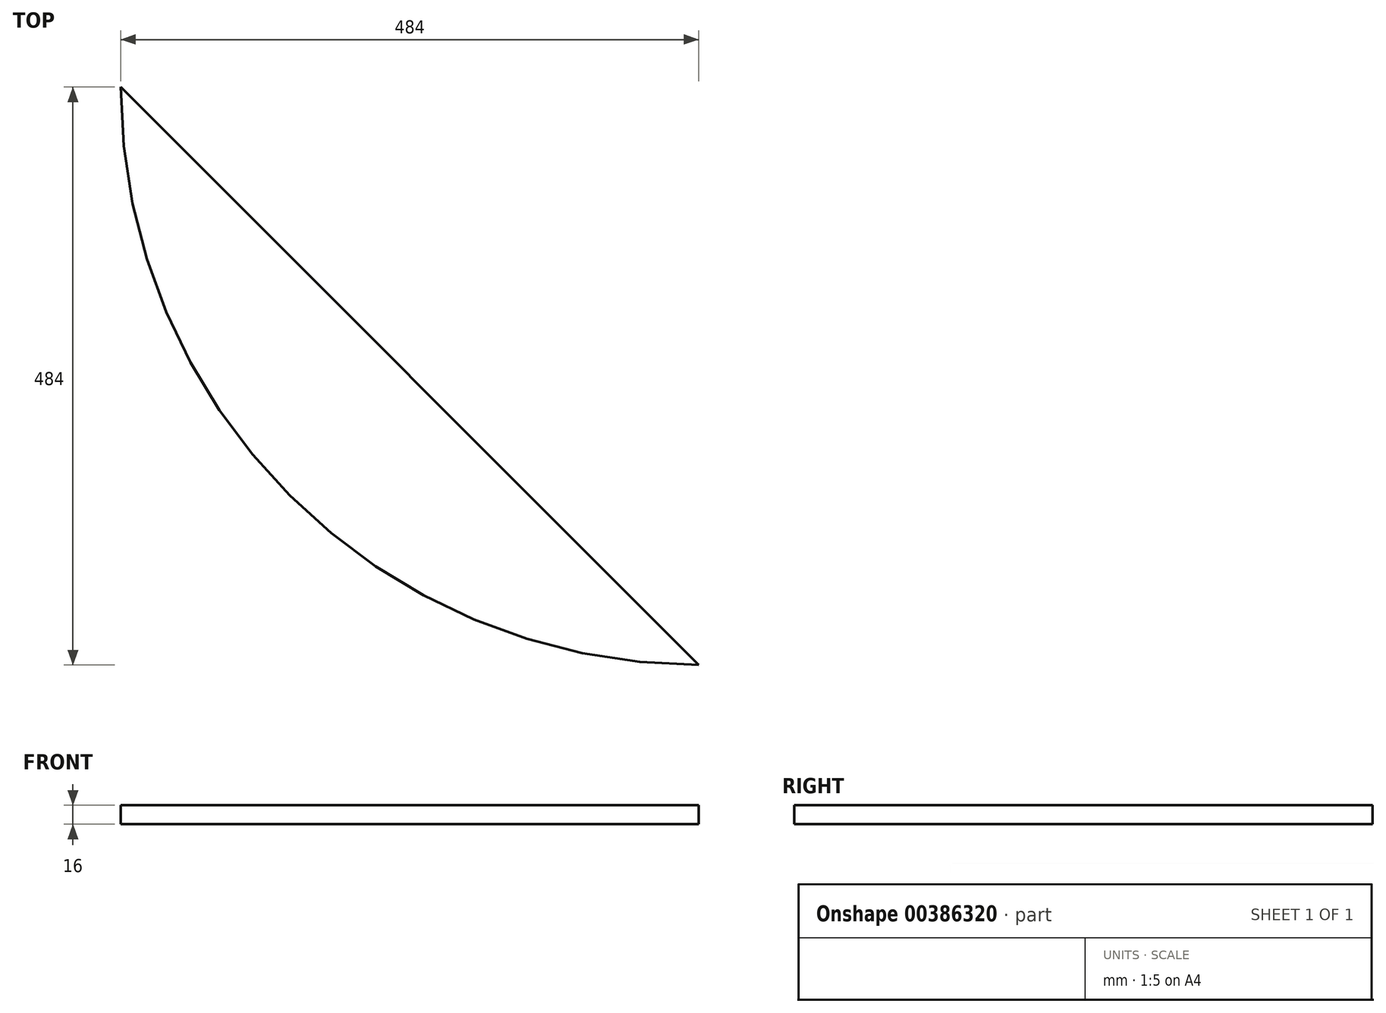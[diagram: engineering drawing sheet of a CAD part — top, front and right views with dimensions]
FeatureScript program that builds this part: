
annotation { "Feature Type Name" : "Feature", "Feature Type Description" : "" }
export const myFeature = defineFeature(function(context is Context, id is Id, definition is map)
    precondition{}
    {
        {
            var Q0;
            Q0=qCreatedBy(makeId("Top.planeOp"),FACE);
            var sketch = newSketch(context, id + "F0", { "sketchPlane" : qUnion([Q0])});
            skCircle(sketch, "E0", {"center": v(-41.67, 0) * mm, "radius": 500 * mm});
            skCircle(sketch, "E1", {"center": v(-41.67, 0) * mm, "radius": 484 * mm});
            skCircle(sketch, "E2.cCircle", {"center": v(-41.67, 0) * mm, "radius": 484 * mm, "construction": true});
            skLineSegment(sketch, "E2.0", {"start": v(-41.67, 484) * mm, "end": v(442.33, 0) * mm});
            skLineSegment(sketch, "E2.1", {"start": v(442.33, 0) * mm, "end": v(-41.67, -484) * mm});
            skLineSegment(sketch, "E2.2", {"start": v(-41.67, -484) * mm, "end": v(-525.67, 0) * mm});
            skLineSegment(sketch, "E2.3", {"start": v(-525.67, 0) * mm, "end": v(-41.67, 484) * mm});
            skLineSegment(sketch, "E3", {"start": v(-41.67, 484) * mm, "end": v(-41.67, -484) * mm});
            skLineSegment(sketch, "E4", {"start": v(-525.67, 0) * mm, "end": v(442.33, 0) * mm});
            skLineSegment(sketch, "E5", {"start": v(-525.67, 0) * mm, "end": v(-541.67, 0) * mm});
            skLineSegment(sketch, "E6", {"start": v(-41.67, 484) * mm, "end": v(-41.67, 500) * mm});
            skLineSegment(sketch, "E7", {"start": v(-41.67, -484) * mm, "end": v(-41.67, -500) * mm});
            skLineSegment(sketch, "E8", {"start": v(442.33, 0) * mm, "end": v(458.33, 0) * mm});
            skLineSegment(sketch, "E9.2", {"start": v(442.33, 0) * mm, "end": v(-41.67, 484) * mm});
            skLineSegment(sketch, "E10.bottom", {"start": v(-525.67, 0) * mm, "end": v(-41.67, 0) * mm});
            skLineSegment(sketch, "E10.right", {"start": v(-41.67, 0) * mm, "end": v(-41.67, 484) * mm});
            skLineSegment(sketch, "E11.right", {"start": v(-41.67, 0) * mm, "end": v(-41.67, -484) * mm});
            skLineSegment(sketch, "E12.bottom", {"start": v(-41.67, 0) * mm, "end": v(458.33, 0) * mm});
            skLineSegment(sketch, "E12.top", {"start": v(-41.67, 0) * mm, "end": v(458.33, 0) * mm});
            skLineSegment(sketch, "E12.left", {"start": v(-41.67, 0) * mm, "end": v(-41.67, 0) * mm});
            skLineSegment(sketch, "E12.right", {"start": v(458.33, 0) * mm, "end": v(458.33, 0) * mm});
            skLineSegment(sketch, "E13.top", {"start": v(-41.67, 0) * mm, "end": v(442.33, 0) * mm});
            skLineSegment(sketch, "E13.left", {"start": v(-41.67, -484) * mm, "end": v(-41.67, 0) * mm});
            skSolve(sketch);
        }
        {
            var Q0;
            {var subQ0=sQuery(id+"F0.wireOp",EDGE,"E2.2");Q0=makeQuery(id+"F0.imprint","IMPRINT",FACE,{"disambiguationData":[TD([[makeQuery(id+"F0.imprint","IMPRINT",EDGE,{"derivedFrom":subQ0}),1.0]])]});}
            extrude(context, id + "F1", {"entities" : qUnion([Q0]), "depth" : 16 * mm});
        }
    });
